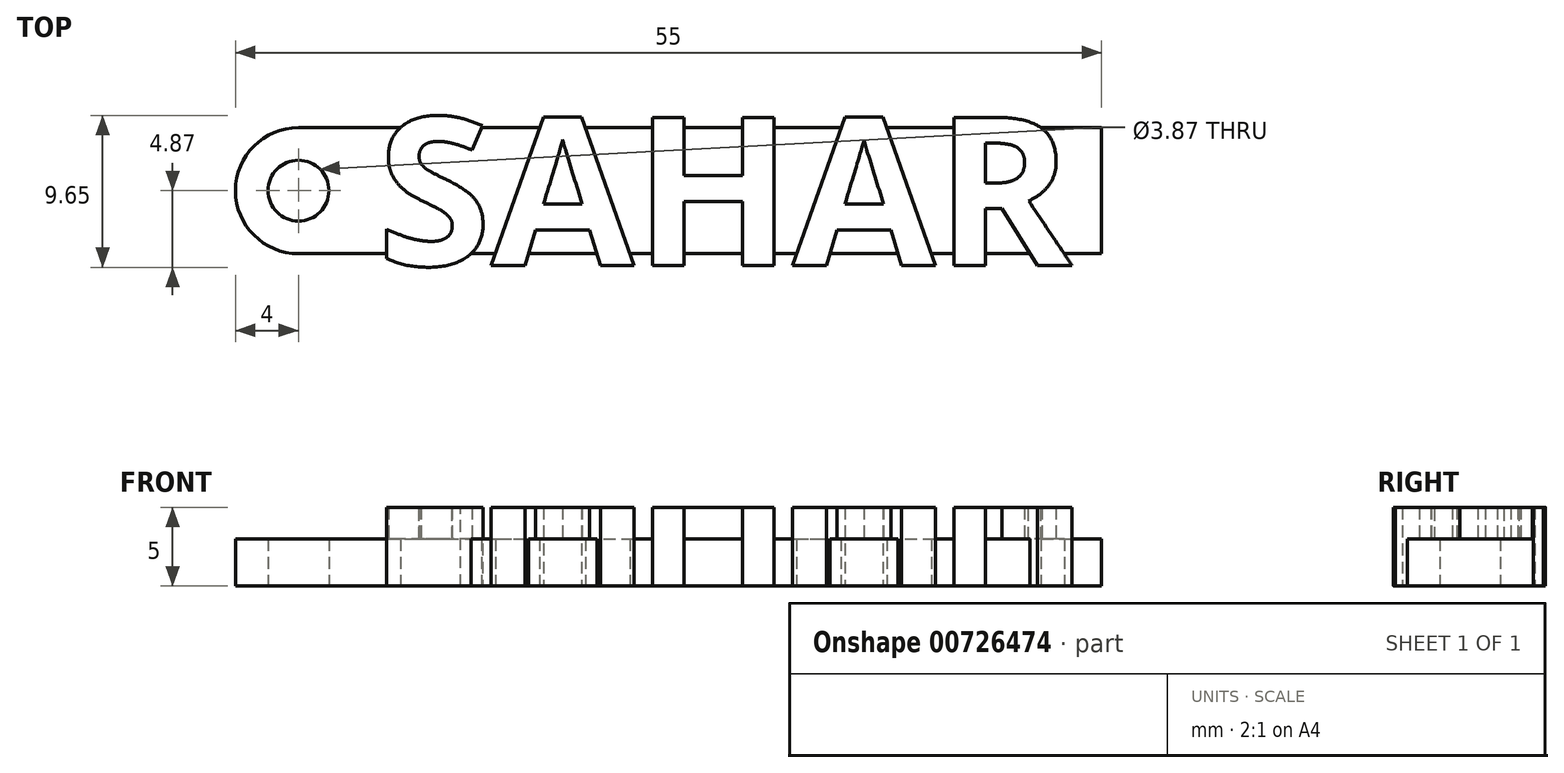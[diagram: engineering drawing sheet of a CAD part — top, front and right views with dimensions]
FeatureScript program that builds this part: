
annotation { "Feature Type Name" : "Feature", "Feature Type Description" : "" }
export const myFeature = defineFeature(function(context is Context, id is Id, definition is map)
    precondition{}
    {
        {
            var Q0;
            Q0=qCreatedBy(makeId("Top.planeOp"),FACE);
            var sketch = newSketch(context, id + "F0", { "sketchPlane" : qUnion([Q0])});
            skLineSegment(sketch, "E0.bottom", {"start": v(-23.5, 4) * mm, "end": v(23.5, 4) * mm});
            skLineSegment(sketch, "E0.top", {"start": v(-23.5, -4) * mm, "end": v(23.5, -4) * mm});
            skLineSegment(sketch, "E0.left", {"start": v(-23.5, 4) * mm, "end": v(-23.5, -4) * mm});
            skLineSegment(sketch, "E0.right", {"start": v(23.5, 4) * mm, "end": v(23.5, -4) * mm});
            skPoint(sketch, "E0.middle", {"position": v(0, 0) * mm});
            skText(sketch, "E1", { "text": "SAHAR", "fontName": "OpenSans-Bold.ttf"});
            skPoint(sketch, "E2", {"position": v(0, 4) * mm});
            skLineSegment(sketch, "E3", {"start": v(-23.5, 4) * mm, "end": v(-31.5, 4) * mm});
            skLineSegment(sketch, "E4", {"start": v(-31.5, 4) * mm, "end": v(-31.5, -4) * mm});
            skLineSegment(sketch, "E5", {"start": v(-31.5, -4) * mm, "end": v(-23.5, -4) * mm});
            skLineSegment(sketch, "E6", {"start": v(-27.5, 4) * mm, "end": v(-27.5, -4) * mm});
            skArc(sketch, "E7", {"start": v(-27.5, 4) * mm, "mid": v(-31.5, 0) * mm, "end": v(-27.5, -4) * mm});
            skCircle(sketch, "E8", {"center": v(-27.5, 0) * mm, "radius": 1.93 * mm});
            const initialGuessF0  = {"E1": [-0.0225, -0.00474, 1, 0, 0.00947]};
            skSetInitialGuess(sketch, initialGuessF0);
            skSolve(sketch);
        }
        {
            var Q0;
            {var subQ0=sQuery(id+"F0.wireOp",EDGE,"E1.sketch_text.stroke-34");var subQ1=sQuery(id+"F0.wireOp",EDGE,"E0.bottom");var subQ2=makeQuery(id+"F0.imprint","INTERSECT",VERTEX,{"derivedFrom":[subQ1,subQ0]});Q0=makeQuery(id+"F0.imprint","IMPRINT",FACE,{"disambiguationData":[TD([[makeQuery(id+"F0.imprint","IMPRINT",EDGE,{"disambiguationData":[TD([[subQ2,-1.0]])],"derivedFrom":subQ1}),-1.0]])]});}
            var Q1;
            {var subQ5=sQuery(id+"F0.wireOp",EDGE,"E1.sketch_text.stroke-48");Q1=makeQuery(id+"F0.imprint","IMPRINT",FACE,{"disambiguationData":[TD([[makeQuery(id+"F0.imprint","IMPRINT",EDGE,{"derivedFrom":subQ5}),1.0]])]});}
            var Q2;
            {var subQ5=sQuery(id+"F0.wireOp",EDGE,"E1.sketch_text.stroke-42");Q2=makeQuery(id+"F0.imprint","IMPRINT",FACE,{"disambiguationData":[TD([[makeQuery(id+"F0.imprint","IMPRINT",EDGE,{"derivedFrom":subQ5}),1.0]])]});}
            var Q3;
            {var subQ0=sQuery(id+"F0.wireOp",EDGE,"E1.sketch_text.stroke-51");var subQ1=sQuery(id+"F0.wireOp",EDGE,"E0.bottom");var subQ2=makeQuery(id+"F0.imprint","INTERSECT",VERTEX,{"derivedFrom":[subQ1,subQ0]});Q3=makeQuery(id+"F0.imprint","IMPRINT",FACE,{"disambiguationData":[TD([[makeQuery(id+"F0.imprint","IMPRINT",EDGE,{"disambiguationData":[TD([[subQ2,-1.0]])],"derivedFrom":subQ1}),-1.0]])]});}
            var Q4;
            Q4=makeQuery(id+"F0.imprint","IMPRINT",FACE,{"disambiguationData":[TD([[makeQuery(id+"F0.imprint","IMPRINT",EDGE,{"derivedFrom":sQuery(id+"F0.wireOp",EDGE,"E1.sketch_text.stroke-60")}),1.0]])]});
            var Q5;
            {var subQ5=sQuery(id+"F0.wireOp",EDGE,"E1.sketch_text.stroke-53");Q5=makeQuery(id+"F0.imprint","IMPRINT",FACE,{"disambiguationData":[TD([[makeQuery(id+"F0.imprint","IMPRINT",EDGE,{"derivedFrom":subQ5}),1.0]])]});}
            var Q6;
            {var subQ0=sQuery(id+"F0.wireOp",EDGE,"E1.sketch_text.stroke-58");var subQ1=sQuery(id+"F0.wireOp",EDGE,"E0.bottom");var subQ2=makeQuery(id+"F0.imprint","INTERSECT",VERTEX,{"derivedFrom":[subQ1,subQ0]});Q6=makeQuery(id+"F0.imprint","IMPRINT",FACE,{"disambiguationData":[TD([[makeQuery(id+"F0.imprint","IMPRINT",EDGE,{"disambiguationData":[TD([[subQ2,-1.0]])],"derivedFrom":subQ1}),-1.0]])]});}
            var Q7;
            Q7=makeQuery(id+"F0.imprint","IMPRINT",FACE,{"disambiguationData":[TD([[makeQuery(id+"F0.imprint","IMPRINT",EDGE,{"derivedFrom":sQuery(id+"F0.wireOp",EDGE,"E1.sketch_text.stroke-64")}),1.0]])]});
            var Q8;
            {var subQ5=sQuery(id+"F0.wireOp",EDGE,"E1.sketch_text.stroke-82");Q8=makeQuery(id+"F0.imprint","IMPRINT",FACE,{"disambiguationData":[TD([[makeQuery(id+"F0.imprint","IMPRINT",EDGE,{"derivedFrom":subQ5}),1.0]])]});}
            var Q9;
            {var subQ0=sQuery(id+"F0.wireOp",EDGE,"E0.right");Q9=makeQuery(id+"F0.imprint","IMPRINT",FACE,{"disambiguationData":[TD([[makeQuery(id+"F0.imprint","IMPRINT",EDGE,{"derivedFrom":subQ0}),-1.0]])]});}
            var Q10;
            {var subQ5=sQuery(id+"F0.wireOp",EDGE,"E1.sketch_text.stroke-29");Q10=makeQuery(id+"F0.imprint","IMPRINT",FACE,{"disambiguationData":[TD([[makeQuery(id+"F0.imprint","IMPRINT",EDGE,{"derivedFrom":subQ5}),1.0]])]});}
            var Q11;
            Q11=makeQuery(id+"F0.imprint","IMPRINT",FACE,{"disambiguationData":[TD([[makeQuery(id+"F0.imprint","IMPRINT",EDGE,{"derivedFrom":sQuery(id+"F0.wireOp",EDGE,"E1.sketch_text.stroke-36")}),1.0]])]});
            var Q12;
            {var subQ5=sQuery(id+"F0.wireOp",EDGE,"E1.sketch_text.stroke-19");Q12=makeQuery(id+"F0.imprint","IMPRINT",FACE,{"disambiguationData":[TD([[makeQuery(id+"F0.imprint","IMPRINT",EDGE,{"derivedFrom":subQ5}),1.0]])]});}
            var Q13;
            {var subQ1=sQuery(id+"F0.wireOp",EDGE,"E0.left");Q13=makeQuery(id+"F0.imprint","IMPRINT",FACE,{"disambiguationData":[TD([[makeQuery(id+"F0.imprint","IMPRINT",EDGE,{"derivedFrom":subQ1}),1.0]])]});}
            var Q14;
            {var subQ6=sQuery(id+"F0.wireOp",EDGE,"E0.left");Q14=makeQuery(id+"F0.imprint","IMPRINT",FACE,{"disambiguationData":[TD([[makeQuery(id+"F0.imprint","IMPRINT",EDGE,{"derivedFrom":subQ6}),-1.0]])]});}
            var Q15;
            {var subQ1=sQuery(id+"F0.wireOp",EDGE,"E6");var subQ5=sQuery(id+"F0.wireOp",EDGE,"E8");var subQ7=makeQuery(id+"F0.imprint","INTERSECT",VERTEX,{"disambiguationData":[OD(0.0)],"derivedFrom":[subQ1,subQ5]});Q15=makeQuery(id+"F0.imprint","IMPRINT",FACE,{"disambiguationData":[TD([[makeQuery(id+"F0.imprint","IMPRINT",EDGE,{"disambiguationData":[TD([[subQ7,-1.0]])],"derivedFrom":subQ5}),-1.0]])]});}
            extrude(context, id + "F1", {"entities" : qUnion([Q0, Q1, Q2, Q3, Q4, Q5, Q6, Q7, Q8, Q9, Q10, Q11, Q12, Q13, Q14, Q15]), "depth" : 3 * mm, "offsetDistance" : 25 * mm});
        }
        {
            var Q0;
            {var subQ12=sQuery(id+"F0.wireOp",EDGE,"E1.sketch_text.stroke-4");Q0=makeQuery(id+"F0.imprint","IMPRINT",FACE,{"disambiguationData":[TD([[makeQuery(id+"F0.imprint","IMPRINT",EDGE,{"derivedFrom":subQ12}),-1.0]])]});}
            var Q1;
            {var subQ0=sQuery(id+"F0.wireOp",EDGE,"E1.sketch_text.stroke-15");Q1=makeQuery(id+"F0.imprint","IMPRINT",FACE,{"disambiguationData":[TD([[makeQuery(id+"F0.imprint","IMPRINT",EDGE,{"derivedFrom":subQ0}),-1.0]])]});}
            var Q2;
            {var subQ1=sQuery(id+"F0.wireOp",EDGE,"E1.sketch_text.stroke-1");Q2=makeQuery(id+"F0.imprint","IMPRINT",FACE,{"disambiguationData":[TD([[makeQuery(id+"F0.imprint","IMPRINT",EDGE,{"derivedFrom":subQ1}),-1.0]])]});}
            var Q3;
            {var subQ5=sQuery(id+"F0.wireOp",EDGE,"E1.sketch_text.stroke-31");Q3=makeQuery(id+"F0.imprint","IMPRINT",FACE,{"disambiguationData":[TD([[makeQuery(id+"F0.imprint","IMPRINT",EDGE,{"derivedFrom":subQ5}),-1.0]])]});}
            var Q4;
            {var subQ5=sQuery(id+"F0.wireOp",EDGE,"E1.sketch_text.stroke-29");Q4=makeQuery(id+"F0.imprint","IMPRINT",FACE,{"disambiguationData":[TD([[makeQuery(id+"F0.imprint","IMPRINT",EDGE,{"derivedFrom":subQ5}),-1.0]])]});}
            var Q5;
            {var subQ5=sQuery(id+"F0.wireOp",EDGE,"E1.sketch_text.stroke-33");Q5=makeQuery(id+"F0.imprint","IMPRINT",FACE,{"disambiguationData":[TD([[makeQuery(id+"F0.imprint","IMPRINT",EDGE,{"derivedFrom":subQ5}),-1.0]])]});}
            var Q6;
            {var subQ5=sQuery(id+"F0.wireOp",EDGE,"E1.sketch_text.stroke-35");Q6=makeQuery(id+"F0.imprint","IMPRINT",FACE,{"disambiguationData":[TD([[makeQuery(id+"F0.imprint","IMPRINT",EDGE,{"derivedFrom":subQ5}),-1.0]])]});}
            var Q7;
            {var subQ5=sQuery(id+"F0.wireOp",EDGE,"E1.sketch_text.stroke-44");Q7=makeQuery(id+"F0.imprint","IMPRINT",FACE,{"disambiguationData":[TD([[makeQuery(id+"F0.imprint","IMPRINT",EDGE,{"derivedFrom":subQ5}),-1.0]])]});}
            var Q8;
            {var subQ8=sQuery(id+"F0.wireOp",EDGE,"E1.sketch_text.stroke-42");Q8=makeQuery(id+"F0.imprint","IMPRINT",FACE,{"disambiguationData":[TD([[makeQuery(id+"F0.imprint","IMPRINT",EDGE,{"derivedFrom":subQ8}),-1.0]])]});}
            var Q9;
            {var subQ5=sQuery(id+"F0.wireOp",EDGE,"E1.sketch_text.stroke-46");Q9=makeQuery(id+"F0.imprint","IMPRINT",FACE,{"disambiguationData":[TD([[makeQuery(id+"F0.imprint","IMPRINT",EDGE,{"derivedFrom":subQ5}),-1.0]])]});}
            var Q10;
            {var subQ5=sQuery(id+"F0.wireOp",EDGE,"E1.sketch_text.stroke-50");Q10=makeQuery(id+"F0.imprint","IMPRINT",FACE,{"disambiguationData":[TD([[makeQuery(id+"F0.imprint","IMPRINT",EDGE,{"derivedFrom":subQ5}),-1.0]])]});}
            var Q11;
            {var subQ5=sQuery(id+"F0.wireOp",EDGE,"E1.sketch_text.stroke-40");Q11=makeQuery(id+"F0.imprint","IMPRINT",FACE,{"disambiguationData":[TD([[makeQuery(id+"F0.imprint","IMPRINT",EDGE,{"derivedFrom":subQ5}),-1.0]])]});}
            var Q12;
            {var subQ5=sQuery(id+"F0.wireOp",EDGE,"E1.sketch_text.stroke-55");Q12=makeQuery(id+"F0.imprint","IMPRINT",FACE,{"disambiguationData":[TD([[makeQuery(id+"F0.imprint","IMPRINT",EDGE,{"derivedFrom":subQ5}),-1.0]])]});}
            var Q13;
            {var subQ11=sQuery(id+"F0.wireOp",EDGE,"E1.sketch_text.stroke-53");Q13=makeQuery(id+"F0.imprint","IMPRINT",FACE,{"disambiguationData":[TD([[makeQuery(id+"F0.imprint","IMPRINT",EDGE,{"derivedFrom":subQ11}),-1.0]])]});}
            var Q14;
            {var subQ5=sQuery(id+"F0.wireOp",EDGE,"E1.sketch_text.stroke-57");Q14=makeQuery(id+"F0.imprint","IMPRINT",FACE,{"disambiguationData":[TD([[makeQuery(id+"F0.imprint","IMPRINT",EDGE,{"derivedFrom":subQ5}),-1.0]])]});}
            var Q15;
            {var subQ5=sQuery(id+"F0.wireOp",EDGE,"E1.sketch_text.stroke-59");Q15=makeQuery(id+"F0.imprint","IMPRINT",FACE,{"disambiguationData":[TD([[makeQuery(id+"F0.imprint","IMPRINT",EDGE,{"derivedFrom":subQ5}),-1.0]])]});}
            var Q16;
            {var subQ5=sQuery(id+"F0.wireOp",EDGE,"E1.sketch_text.stroke-72");Q16=makeQuery(id+"F0.imprint","IMPRINT",FACE,{"disambiguationData":[TD([[makeQuery(id+"F0.imprint","IMPRINT",EDGE,{"derivedFrom":subQ5}),-1.0]])]});}
            var Q17;
            Q17=makeQuery(id+"F0.imprint","IMPRINT",FACE,{"disambiguationData":[TD([[makeQuery(id+"F0.imprint","IMPRINT",EDGE,{"derivedFrom":sQuery(id+"F0.wireOp",EDGE,"E1.sketch_text.stroke-64")}),-1.0]])]});
            var Q18;
            {var subQ5=sQuery(id+"F0.wireOp",EDGE,"E1.sketch_text.stroke-74");Q18=makeQuery(id+"F0.imprint","IMPRINT",FACE,{"disambiguationData":[TD([[makeQuery(id+"F0.imprint","IMPRINT",EDGE,{"derivedFrom":subQ5}),-1.0]])]});}
            var Q19;
            {var subQ5=sQuery(id+"F0.wireOp",EDGE,"E1.sketch_text.stroke-80");Q19=makeQuery(id+"F0.imprint","IMPRINT",FACE,{"disambiguationData":[TD([[makeQuery(id+"F0.imprint","IMPRINT",EDGE,{"derivedFrom":subQ5}),-1.0]])]});}
            extrude(context, id + "F2", {"entities" : qUnion([Q0, Q1, Q2, Q3, Q4, Q5, Q6, Q7, Q8, Q9, Q10, Q11, Q12, Q13, Q14, Q15, Q16, Q17, Q18, Q19]), "operationType" : NewBodyOperationType.ADD, "depth" : 5 * mm, "offsetDistance" : 25 * mm});
        }
    });
